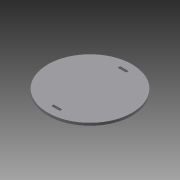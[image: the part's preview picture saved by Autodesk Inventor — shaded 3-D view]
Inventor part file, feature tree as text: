
AUTODESK INVENTOR PART (.ipt)
format: ipt  version: 2015 SP2 (Build 190223200, 223)  size: 87,552 bytes
history: native  units: in
note: dims shown in document units (in); Inventor stores cm internally (conversion verified against a paired STEP export)
features: extrude x2, sketch x2
ambient origin geometry x8: Origin, YZ Plane, XZ Plane, XY Plane, X Axis, Y Axis, Z Axis, Center Point
bodies: Solid1 (feature_tree)
feature tree (4):
  extrude  "Extrusion1"  Depth=0.1181in TaperAngle=0.0deg
  extrude  "Extrusion2"  Depth=0.1181in
  sketch  "Sketch1"  dims[d0=3.937in d1=0.1181in d2=0.0in]
  sketch  "Sketch2"  dims[d3=0.3937in d4=0.1181in d5=0.1969in d6=1.4961in d7=0.3937in d8=0.1181in d9=0.1969in d10=1.4961in d11=0.1181in d12=0.0in]
